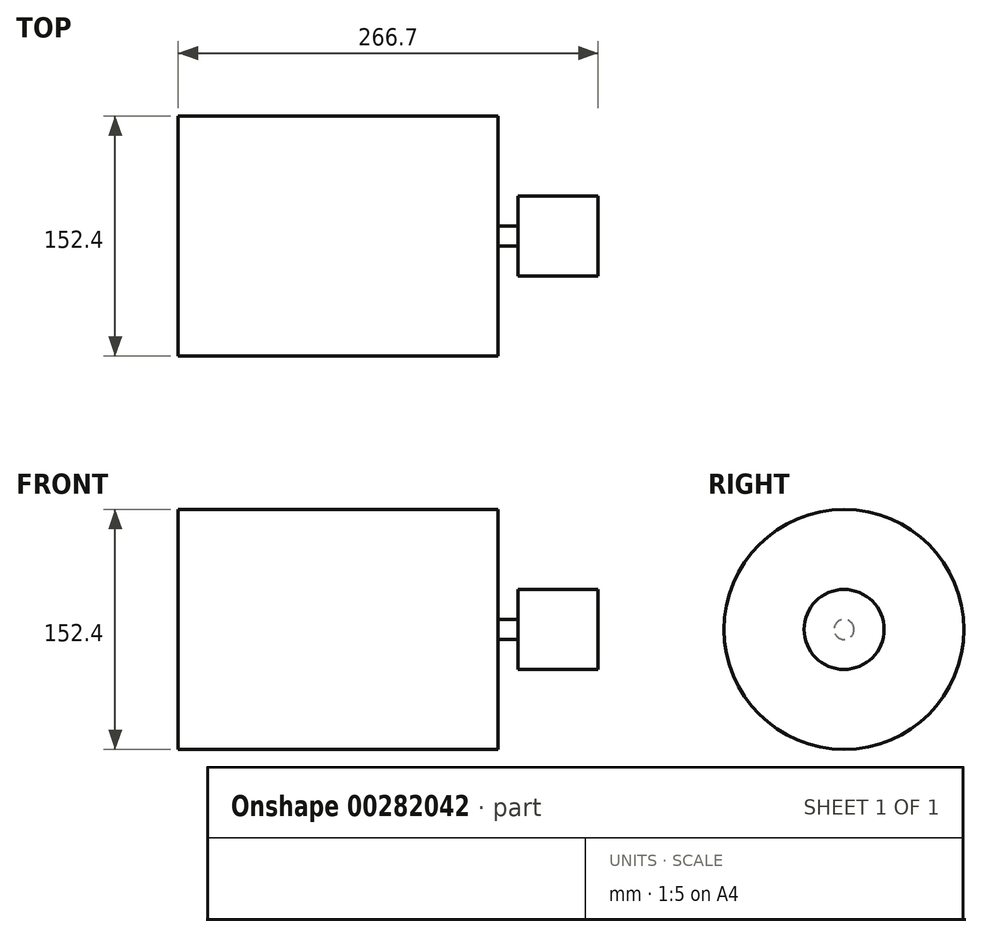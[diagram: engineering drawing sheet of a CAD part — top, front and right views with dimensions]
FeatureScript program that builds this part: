
annotation { "Feature Type Name" : "Feature", "Feature Type Description" : "" }
export const myFeature = defineFeature(function(context is Context, id is Id, definition is map)
    precondition{}
    {
        {
            var Q0;
            Q0=qCreatedBy(makeId("Right.planeOp"),FACE);
            var sketch = newSketch(context, id + "F0", { "sketchPlane" : qUnion([Q0])});
            skCircle(sketch, "E0", {"center": v(0, 0) * mm, "radius": 76.2 * mm});
            skSolve(sketch);
        }
        {
            var Q0;
            Q0 = qSketchRegion(id + "F0", true);
            extrude(context, id + "F1", {"entities" : qUnion([Q0]), "depth" : 203.2 * mm});
        }
        {
            var Q0;
            Q0=makeQuery(id+"F1.opExtrude","CAP_FACE",FACE,{"disambiguationData":[OSD([sQuery(id+"F0.wireOp",EDGE,"E0")])],"isStart":false});
            var sketch = newSketch(context, id + "F2", { "sketchPlane" : qUnion([Q0])});
            skCircle(sketch, "E1", {"center": v(0, 0) * mm, "radius": 6.35 * mm});
            skSolve(sketch);
        }
        {
            var Q0;
            Q0 = qSketchRegion(id + "F2", true);
            extrude(context, id + "F3", {"entities" : qUnion([Q0]), "operationType" : NewBodyOperationType.ADD, "depth" : 12.7 * mm});
        }
        {
            var Q0;
            Q0=makeQuery(id+"F3.opExtrude","CAP_FACE",FACE,{"disambiguationData":[OSD([sQuery(id+"F2.wireOp",EDGE,"E1")])],"isStart":false});
            var sketch = newSketch(context, id + "F4", { "sketchPlane" : qUnion([Q0])});
            skCircle(sketch, "E2", {"center": v(0, 0) * mm, "radius": 25.4 * mm});
            skSolve(sketch);
        }
        {
            var Q0;
            Q0 = qSketchRegion(id + "F4", true);
            extrude(context, id + "F5", {"entities" : qUnion([Q0]), "operationType" : NewBodyOperationType.ADD, "depth" : 50.8 * mm});
        }
    });
